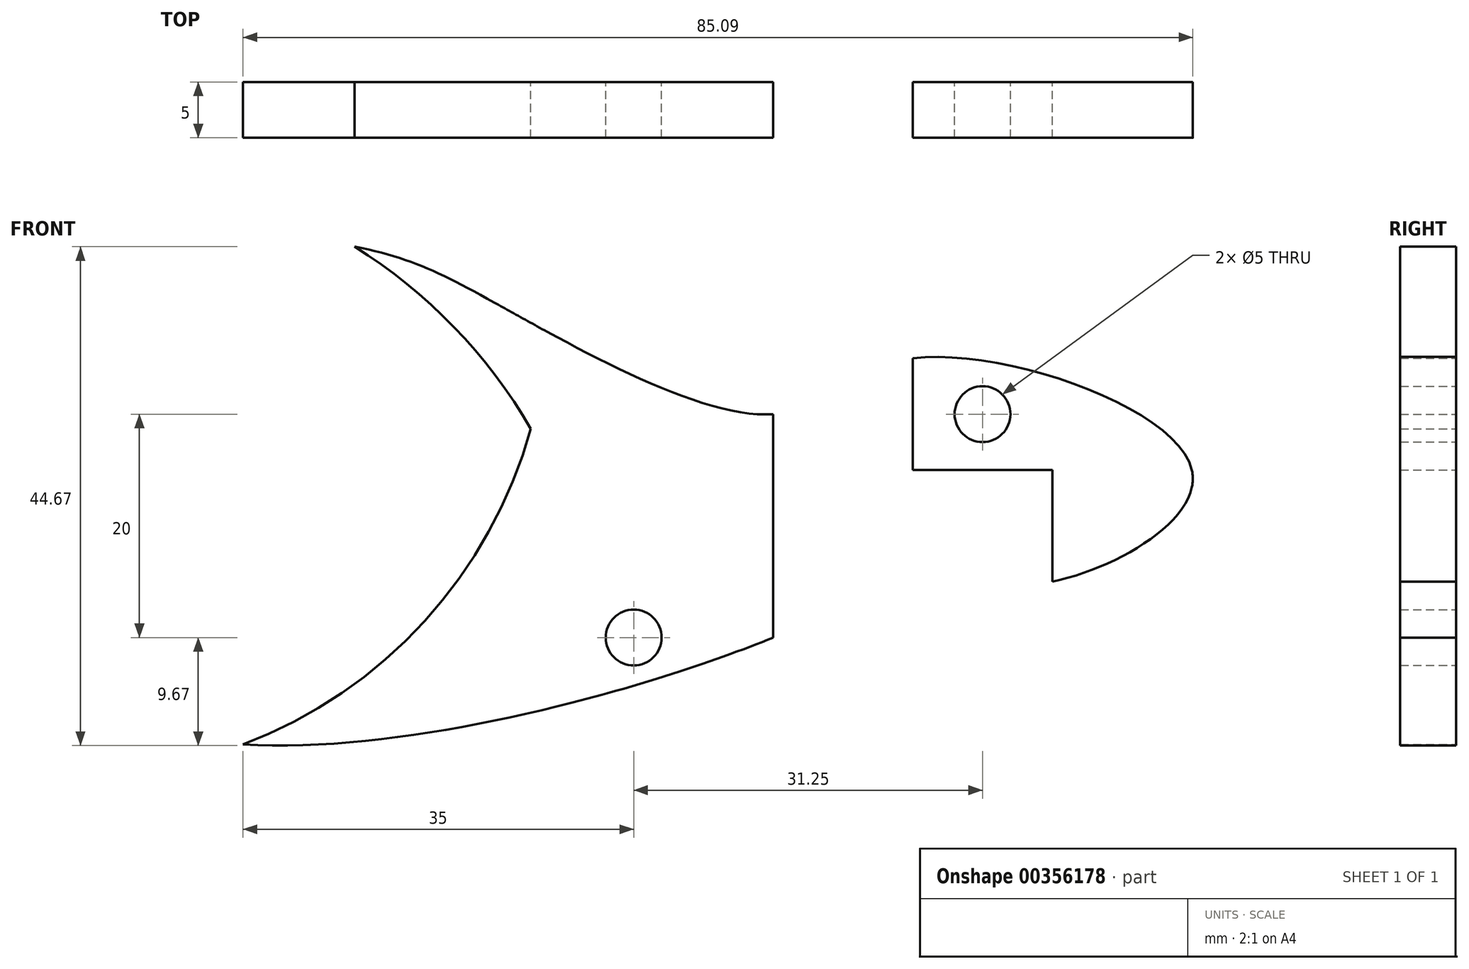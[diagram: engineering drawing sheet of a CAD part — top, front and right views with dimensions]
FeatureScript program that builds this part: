
annotation { "Feature Type Name" : "Feature", "Feature Type Description" : "" }
export const myFeature = defineFeature(function(context is Context, id is Id, definition is map)
    precondition{}
    {
        {
            var Q0;
            Q0=qCreatedBy(makeId("Front.planeOp"),FACE);
            var sketch = newSketch(context, id + "F0", { "sketchPlane" : qUnion([Q0])});
            skLineSegment(sketch, "E0.bottom", {"start": v(-50, 0) * mm, "end": v(50, 0) * mm});
            skLineSegment(sketch, "E0.top", {"start": v(-50, -40) * mm, "end": v(50, -40) * mm});
            skLineSegment(sketch, "E0.left", {"start": v(-50, 0) * mm, "end": v(-50, -40) * mm});
            skLineSegment(sketch, "E0.right", {"start": v(50, 0) * mm, "end": v(50, -40) * mm});
            skLineSegment(sketch, "E1", {"start": v(-50, -40) * mm, "end": v(-35, -40) * mm});
            skLineSegment(sketch, "E2", {"start": v(-50, -40) * mm, "end": v(-50, -30) * mm});
            skLineSegment(sketch, "E3", {"start": v(-50, -30) * mm, "end": v(-35, -30) * mm});
            skLineSegment(sketch, "E4", {"start": v(-35, -30) * mm, "end": v(-35, -40) * mm});
            skCircle(sketch, "E5", {"center": v(-35, -30) * mm, "radius": 2.5 * mm});
            skPoint(sketch, "E6", {"position": v(-45, -10) * mm});
            skLineSegment(sketch, "E7.bottom", {"start": v(-45, -10) * mm, "end": v(-50, -10) * mm});
            skLineSegment(sketch, "E7.top", {"start": v(-45, 0) * mm, "end": v(-50, 0) * mm});
            skLineSegment(sketch, "E7.left", {"start": v(-45, -10) * mm, "end": v(-45, 0) * mm});
            skLineSegment(sketch, "E7.right", {"start": v(-50, -10) * mm, "end": v(-50, 0) * mm});
            skCircle(sketch, "E8", {"center": v(-45, -10) * mm, "radius": 2.5 * mm});
            skPoint(sketch, "E9", {"position": v(0, 0) * mm});
            skPoint(sketch, "E10", {"position": v(50, -20) * mm});
            skLineSegment(sketch, "E11", {"start": v(0, 0) * mm, "end": v(50, 0) * mm});
            skPoint(sketch, "E12", {"position": v(25, 0) * mm});
            skLineSegment(sketch, "E13", {"start": v(25, 0) * mm, "end": v(25, -40) * mm});
            skPoint(sketch, "E14", {"position": v(25, -20) * mm});
            skLineSegment(sketch, "E15", {"start": v(25, -20) * mm, "end": v(50, -20) * mm});
            skPoint(sketch, "E16", {"position": v(37.5, -20) * mm});
            skLineSegment(sketch, "E17", {"start": v(37.5, -20) * mm, "end": v(37.5, -40) * mm});
            skPoint(sketch, "E18", {"position": v(37.5, -30) * mm});
            skLineSegment(sketch, "E19", {"start": v(-50, 0) * mm, "end": v(0, 0) * mm});
            skPoint(sketch, "E20", {"position": v(-25, 0) * mm});
            skLineSegment(sketch, "E21", {"start": v(25, 0) * mm, "end": v(25, -20) * mm});
            skPoint(sketch, "E22", {"position": v(25, -10) * mm});
            skLineSegment(sketch, "E23", {"start": v(0, 0) * mm, "end": v(25, 0) * mm});
            skPoint(sketch, "E24", {"position": v(12.5, 0) * mm});
            skPoint(sketch, "E25", {"position": v(12.5, -10) * mm});
            skLineSegment(sketch, "E26", {"start": v(12.5, -10) * mm, "end": v(12.5, -20) * mm});
            skPoint(sketch, "E27", {"position": v(12.5, -15) * mm});
            skPoint(sketch, "E28", {"position": v(25, -30) * mm});
            skLineSegment(sketch, "E29", {"start": v(25, -30) * mm, "end": v(25, -40) * mm});
            skPoint(sketch, "E30", {"position": v(25, -35) * mm});
            skPoint(sketch, "E31", {"position": v(12.5, -35) * mm});
            skLineSegment(sketch, "E32", {"start": v(-25, 0) * mm, "end": v(-25, -40) * mm});
            skPoint(sketch, "E33", {"position": v(-50, -20) * mm});
            skLineSegment(sketch, "E34", {"start": v(25, -20) * mm, "end": v(25, -30) * mm});
            skPoint(sketch, "E35", {"position": v(25, -25) * mm});
            skLineSegment(sketch, "E36", {"start": v(-25, 0) * mm, "end": v(0, 0) * mm});
            skPoint(sketch, "E37", {"position": v(-12.5, 0) * mm});
            skPoint(sketch, "E38", {"position": v(-50, -5) * mm});
            skLineSegment(sketch, "E39", {"start": v(-50, -5) * mm, "end": v(-12.5, -5) * mm});
            skFitSpline(sketch, "E40", {"points": [v(12.5, -35) * mm, v(25, -30) * mm, v(37.5, -30) * mm, v(50, -20) * mm, v(25, -10) * mm, v(12.5, -15) * mm, v(-12.5, -5) * mm, v(-25, 0) * mm, v(-50, -5) * mm, v(-50, -40) * mm, v(12.5, -35) * mm]});
            skLineSegment(sketch, "E41", {"start": v(25, -10) * mm, "end": v(37.5, -20) * mm});
            skPoint(sketch, "E42", {"position": v(31.25, -15) * mm});
            skCircle(sketch, "E43", {"center": v(31.25, -15) * mm, "radius": 2.5 * mm});
            skArc(sketch, "E44", {"start": v(-2.83, -40.12) * mm, "mid": v(-8.71, -17.19) * mm, "end": v(-25, 0) * mm});
            skLineSegment(sketch, "E45", {"start": v(12.5, -20) * mm, "end": v(12.5, -35) * mm});
            skLineSegment(sketch, "E46", {"start": v(-35, -30) * mm, "end": v(12.5, -30) * mm});
            skPoint(sketch, "E47", {"position": v(0, -35) * mm});
            skCircle(sketch, "E48", {"center": v(0, -35) * mm, "radius": 2.5 * mm});
            skLineSegment(sketch, "E49", {"start": v(-35, -40) * mm, "end": v(-35, -44.58) * mm});
            skArc(sketch, "E50", {"start": v(-35, -44.58) * mm, "mid": v(-13.8, -26.95) * mm, "end": v(-7.97, 0) * mm});
            skPoint(sketch, "E51", {"position": v(0, -30) * mm});
            skSolve(sketch);
        }
        {
            var Q0;
            {var subQ0=sQuery(id+"F0.wireOp",EDGE,"E40");var subQ1=sQuery(id+"F0.wireOp",EDGE,"E0.right");var subQ3=makeQuery(id+"F0.imprint","INTERSECT",VERTEX,{"derivedFrom":[subQ1,subQ0]});Q0=makeQuery(id+"F0.imprint","IMPRINT",FACE,{"disambiguationData":[TD([[makeQuery(id+"F0.imprint","IMPRINT",EDGE,{"disambiguationData":[TD([[subQ3,1.0]])],"derivedFrom":subQ1}),1.0]])]});}
            var Q1;
            {var subQ0=sQuery(id+"F0.wireOp",EDGE,"E40");var subQ3=sQuery(id+"F0.wireOp",EDGE,"E39");var subQ5=makeQuery(id+"F0.imprint","INTERSECT",VERTEX,{"derivedFrom":[subQ3,subQ0]});Q1=makeQuery(id+"F0.imprint","IMPRINT",FACE,{"disambiguationData":[TD([[makeQuery(id+"F0.imprint","IMPRINT",EDGE,{"disambiguationData":[TD([[subQ5,1.0]])],"derivedFrom":subQ3}),1.0]])]});}
            var Q2;
            {var subQ0=sQuery(id+"F0.wireOp",EDGE,"E40");var subQ2=sQuery(id+"F0.wireOp",EDGE,"E0.right");var subQ4=makeQuery(id+"F0.imprint","INTERSECT",VERTEX,{"derivedFrom":[subQ2,subQ0]});Q2=makeQuery(id+"F0.imprint","IMPRINT",FACE,{"disambiguationData":[TD([[makeQuery(id+"F0.imprint","IMPRINT",EDGE,{"disambiguationData":[TD([[subQ4,1.0]])],"derivedFrom":subQ0}),1.0]])]});}
            var Q3;
            {var subQ0=sQuery(id+"F0.wireOp",EDGE,"E41");var subQ3=sQuery(id+"F0.wireOp",EDGE,"E43");var subQ7=makeQuery(id+"F0.imprint","INTERSECT",VERTEX,{"disambiguationData":[OD(0.0)],"derivedFrom":[subQ0,subQ3]});Q3=makeQuery(id+"F0.imprint","IMPRINT",FACE,{"disambiguationData":[TD([[makeQuery(id+"F0.imprint","IMPRINT",EDGE,{"disambiguationData":[TD([[subQ7,1.0]])],"derivedFrom":subQ3}),-1.0]])]});}
            var Q4;
            {var subQ8=sQuery(id+"F0.wireOp",EDGE,"E34");Q4=makeQuery(id+"F0.imprint","IMPRINT",FACE,{"disambiguationData":[TD([[makeQuery(id+"F0.imprint","IMPRINT",EDGE,{"derivedFrom":subQ8}),-1.0]])]});}
            var Q5;
            {var subQ0=sQuery(id+"F0.wireOp",EDGE,"E41");var subQ3=sQuery(id+"F0.wireOp",EDGE,"E43");var subQ4=makeQuery(id+"F0.imprint","INTERSECT",VERTEX,{"disambiguationData":[OD(0.0)],"derivedFrom":[subQ0,subQ3]});Q5=makeQuery(id+"F0.imprint","IMPRINT",FACE,{"disambiguationData":[TD([[makeQuery(id+"F0.imprint","IMPRINT",EDGE,{"disambiguationData":[TD([[subQ4,-1.0]])],"derivedFrom":subQ3}),-1.0]])]});}
            var Q6;
            {var subQ0=sQuery(id+"F0.wireOp",EDGE,"E34");Q6=makeQuery(id+"F0.imprint","IMPRINT",FACE,{"disambiguationData":[TD([[makeQuery(id+"F0.imprint","IMPRINT",EDGE,{"derivedFrom":subQ0}),1.0]])]});}
            var Q7;
            {var subQ5=sQuery(id+"F0.wireOp",EDGE,"E45");var subQ6=sQuery(id+"F0.wireOp",EDGE,"E26");var subQ7=makeQuery(id+"F0.imprint","INTERSECT",VERTEX,{"derivedFrom":[subQ6,subQ5]});Q7=makeQuery(id+"F0.imprint","IMPRINT",FACE,{"disambiguationData":[TD([[makeQuery(id+"F0.imprint","IMPRINT",EDGE,{"disambiguationData":[TD([[subQ7,1.0]])],"derivedFrom":subQ6}),-1.0]])]});}
            var Q8;
            {var subQ1=sQuery(id+"F0.wireOp",EDGE,"E40");var subQ5=sQuery(id+"F0.wireOp",EDGE,"E0.top");var subQ6=makeQuery(id+"F0.imprint","INTERSECT",VERTEX,{"derivedFrom":[subQ5,subQ1]});Q8=makeQuery(id+"F0.imprint","IMPRINT",FACE,{"disambiguationData":[TD([[makeQuery(id+"F0.imprint","IMPRINT",EDGE,{"disambiguationData":[TD([[subQ6,1.0]])],"derivedFrom":subQ5}),1.0]])]});}
            var Q9;
            {var subQ0=sQuery(id+"F0.wireOp",EDGE,"E40");var subQ1=sQuery(id+"F0.wireOp",EDGE,"E39");var subQ2=makeQuery(id+"F0.imprint","INTERSECT",VERTEX,{"derivedFrom":[subQ1,subQ0]});Q9=makeQuery(id+"F0.imprint","IMPRINT",FACE,{"disambiguationData":[TD([[makeQuery(id+"F0.imprint","IMPRINT",EDGE,{"disambiguationData":[TD([[subQ2,1.0]])],"derivedFrom":subQ1}),-1.0]])]});}
            var Q10;
            {var subQ0=sQuery(id+"F0.wireOp",EDGE,"E46");var subQ1=sQuery(id+"F0.wireOp",EDGE,"E44");var subQ2=makeQuery(id+"F0.imprint","INTERSECT",VERTEX,{"derivedFrom":[subQ1,subQ0]});Q10=makeQuery(id+"F0.imprint","IMPRINT",FACE,{"disambiguationData":[TD([[makeQuery(id+"F0.imprint","IMPRINT",EDGE,{"disambiguationData":[TD([[subQ2,-1.0]])],"derivedFrom":subQ1}),1.0]])]});}
            var Q11;
            {var subQ0=sQuery(id+"F0.wireOp",EDGE,"E40");var subQ1=sQuery(id+"F0.wireOp",EDGE,"E0.top");var subQ2=makeQuery(id+"F0.imprint","INTERSECT",VERTEX,{"derivedFrom":[subQ1,subQ0]});Q11=makeQuery(id+"F0.imprint","IMPRINT",FACE,{"disambiguationData":[TD([[makeQuery(id+"F0.imprint","IMPRINT",EDGE,{"disambiguationData":[TD([[subQ2,1.0]])],"derivedFrom":subQ1}),-1.0]])]});}
            var Q12;
            {var subQ0=sQuery(id+"F0.wireOp",EDGE,"E50");var subQ1=sQuery(id+"F0.wireOp",EDGE,"E0.top");var subQ2=makeQuery(id+"F0.imprint","INTERSECT",VERTEX,{"derivedFrom":[subQ1,subQ0]});Q12=makeQuery(id+"F0.imprint","IMPRINT",FACE,{"disambiguationData":[TD([[makeQuery(id+"F0.imprint","IMPRINT",EDGE,{"disambiguationData":[TD([[subQ2,-1.0]])],"derivedFrom":subQ1}),1.0]])]});}
            var Q13;
            {var subQ0=sQuery(id+"F0.wireOp",EDGE,"E50");var subQ1=sQuery(id+"F0.wireOp",EDGE,"E0.top");var subQ2=makeQuery(id+"F0.imprint","INTERSECT",VERTEX,{"derivedFrom":[subQ1,subQ0]});Q13=makeQuery(id+"F0.imprint","IMPRINT",FACE,{"disambiguationData":[TD([[makeQuery(id+"F0.imprint","IMPRINT",EDGE,{"disambiguationData":[TD([[subQ2,-1.0]])],"derivedFrom":subQ1}),-1.0]])]});}
            var Q14;
            {var subQ5=sQuery(id+"F0.wireOp",EDGE,"E32");var subQ6=sQuery(id+"F0.wireOp",EDGE,"E0.top");var subQ7=makeQuery(id+"F0.imprint","INTERSECT",VERTEX,{"derivedFrom":[subQ6,subQ5]});Q14=makeQuery(id+"F0.imprint","IMPRINT",FACE,{"disambiguationData":[TD([[makeQuery(id+"F0.imprint","IMPRINT",EDGE,{"disambiguationData":[TD([[subQ7,-1.0]])],"derivedFrom":subQ6}),1.0]])]});}
            extrude(context, id + "F1", {"entities" : qUnion([Q0, Q1, Q2, Q3, Q4, Q5, Q6, Q7, Q8, Q9, Q10, Q11, Q12, Q13, Q14]), "depth" : 5 * mm});
        }
    });
